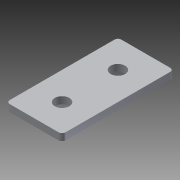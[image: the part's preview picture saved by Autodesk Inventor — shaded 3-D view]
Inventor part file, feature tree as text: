
AUTODESK INVENTOR PART (.ipt)
format: ipt  version: 2014 SP1 (Build 180222100, 222)  size: 91,648 bytes
history: native  units: in
note: dims shown in document units (in); Inventor stores cm internally (conversion verified against a paired STEP export)
features: extrude x1, fillet x1, sketch x1
ambient origin geometry x8: Origin, YZ Plane, XZ Plane, XY Plane, X Axis, Y Axis, Z Axis, Center Point
bodies: Solid1 (feature_tree)
feature tree (3):
  extrude  "Extrusion1"  Depth=1.0in
  fillet  "Fillet1"  Radius=0.26in
  sketch  "Sketch1"  dims[d0=2.0in d1=1.0in d2=0.26in d3=0.26in d4=1.0in d5=0.125in d6=0.0in d7=0.0625in]
